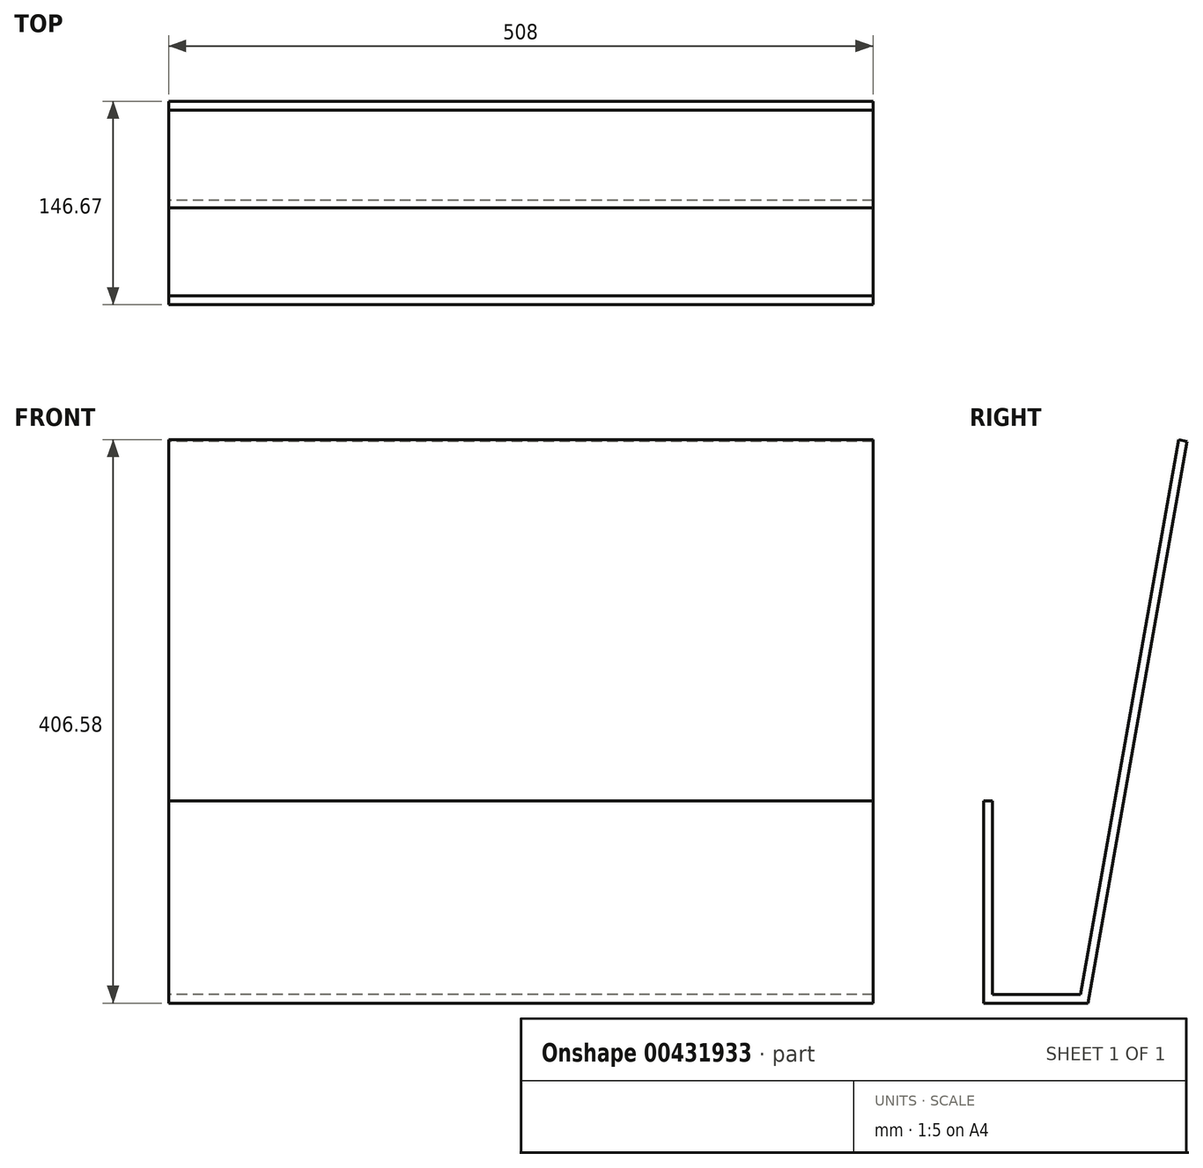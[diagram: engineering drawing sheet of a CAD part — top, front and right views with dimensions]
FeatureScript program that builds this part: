
annotation { "Feature Type Name" : "Feature", "Feature Type Description" : "" }
export const myFeature = defineFeature(function(context is Context, id is Id, definition is map)
    precondition{}
    {
        {
            var Q0;
            Q0=qCreatedBy(makeId("Right.planeOp"),FACE);
            var sketch = newSketch(context, id + "F0", { "sketchPlane" : qUnion([Q0])});
            skLineSegment(sketch, "E0", {"start": v(-63.5, 139.7) * mm, "end": v(-63.5, 0) * mm});
            skLineSegment(sketch, "E1", {"start": v(-63.5, 0) * mm, "end": v(0, 0) * mm});
            skLineSegment(sketch, "E2", {"start": v(0, 0) * mm, "end": v(70.57, 400.23) * mm});
            skLineSegment(sketch, "E3.0", {"start": v(5.33, -6.35) * mm, "end": v(76.82, 399.12) * mm});
            skLineSegment(sketch, "E3.1", {"start": v(-69.85, -6.35) * mm, "end": v(5.33, -6.35) * mm});
            skLineSegment(sketch, "E3.2", {"start": v(-69.85, 139.7) * mm, "end": v(-69.85, -6.35) * mm});
            skLineSegment(sketch, "E4", {"start": v(-69.85, 139.7) * mm, "end": v(-63.5, 139.7) * mm});
            skLineSegment(sketch, "E5", {"start": v(76.82, 399.12) * mm, "end": v(70.57, 400.23) * mm});
            skSolve(sketch);
        }
        {
            var Q0;
            Q0 = qSketchRegion(id + "F0", true);
            extrude(context, id + "F1", {"entities" : qUnion([Q0]), "depth" : 508 * mm});
        }
    });
